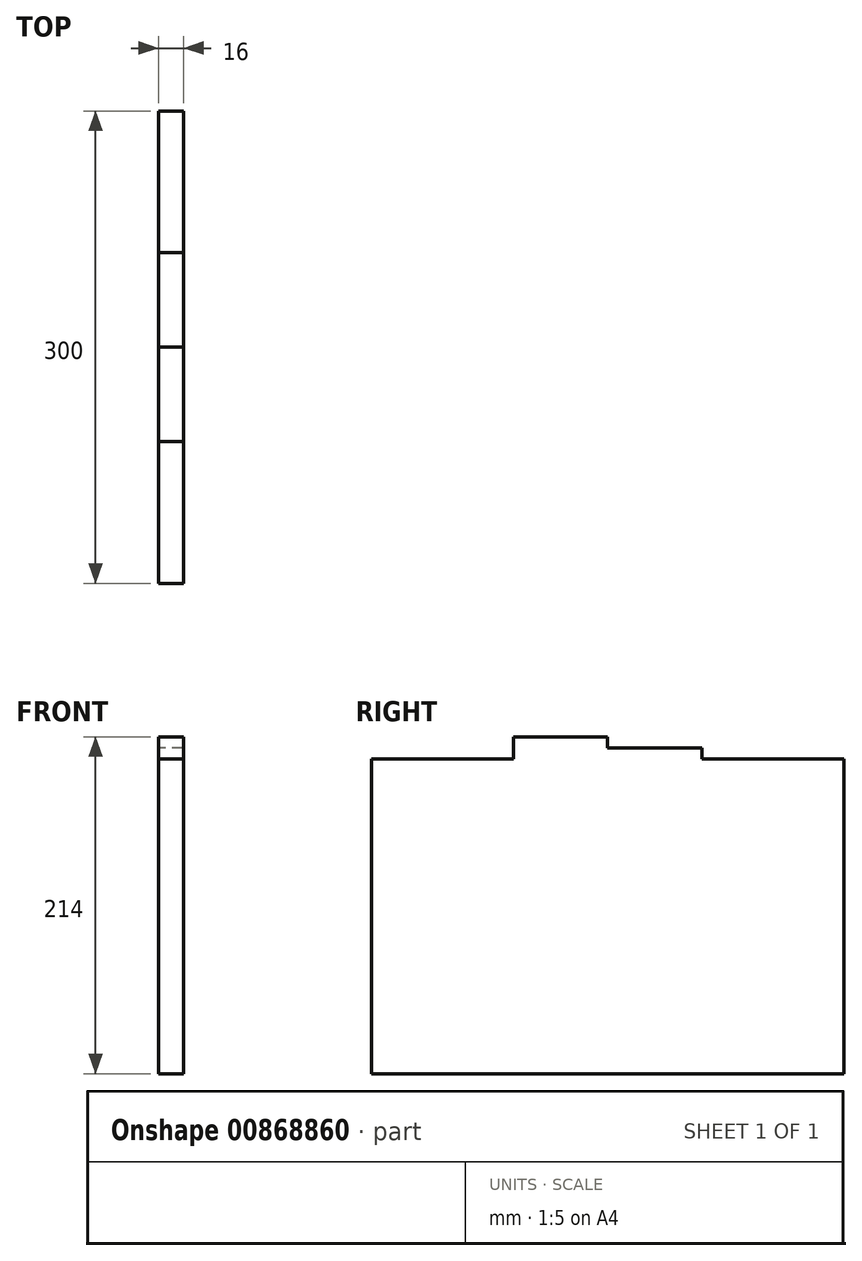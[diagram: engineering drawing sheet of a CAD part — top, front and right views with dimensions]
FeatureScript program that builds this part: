
annotation { "Feature Type Name" : "Feature", "Feature Type Description" : "" }
export const myFeature = defineFeature(function(context is Context, id is Id, definition is map)
    precondition{}
    {
        {
            var Q0;
            Q0=qCreatedBy(makeId("Right.planeOp"),FACE);
            var sketch = newSketch(context, id + "F0", { "sketchPlane" : qUnion([Q0])});
            skLineSegment(sketch, "E0.bottom", {"start": v(0, 0) * mm, "end": v(300, 0) * mm});
            skLineSegment(sketch, "E0.top", {"start": v(0, 200) * mm, "end": v(300, 200) * mm});
            skLineSegment(sketch, "E0.left", {"start": v(0, 0) * mm, "end": v(0, 200) * mm});
            skLineSegment(sketch, "E0.right", {"start": v(300, 0) * mm, "end": v(300, 200) * mm});
            skSolve(sketch);
        }
        {
            var Q0;
            Q0=makeQuery(id+"F0.imprint","IMPRINT",FACE,{"disambiguationData":[TD([[makeQuery(id+"F0.imprint","IMPRINT",EDGE,{"derivedFrom":sQuery(id+"F0.wireOp",EDGE,"E0.bottom")}),1.0]])]});
            extrude(context, id + "F1", {"entities" : qUnion([Q0]), "depth" : 16 * mm, "offsetDistance" : 25 * mm});
        }
        {
            var Q0;
            Q0=makeQuery(id+"F1.opExtrude","CAP_FACE",FACE,{"disambiguationData":[OSD([sQuery(id+"F0.wireOp",EDGE,"E0.bottom"),sQuery(id+"F0.wireOp",EDGE,"E0.top"),sQuery(id+"F0.wireOp",EDGE,"E0.left"),sQuery(id+"F0.wireOp",EDGE,"E0.right")])],"isStart":true});
            var sketch = newSketch(context, id + "F2", { "sketchPlane" : qUnion([Q0])});
            skLineSegment(sketch, "E1", {"start": v(-300, 200) * mm, "end": v(-210, 200) * mm});
            skLineSegment(sketch, "E2", {"start": v(-210, 200) * mm, "end": v(-210, 207) * mm});
            skLineSegment(sketch, "E3", {"start": v(-210, 207) * mm, "end": v(-150, 207) * mm});
            skLineSegment(sketch, "E4", {"start": v(-150, 207) * mm, "end": v(-150, 214) * mm});
            skLineSegment(sketch, "E5", {"start": v(-150, 214) * mm, "end": v(-90, 214) * mm});
            skLineSegment(sketch, "E6", {"start": v(-90, 214) * mm, "end": v(-90, 200) * mm});
            skLineSegment(sketch, "E7", {"start": v(-90, 200) * mm, "end": v(0, 200) * mm});
            skSolve(sketch);
        }
        {
            var Q0;
            {var subQ0=sQuery(id+"F2.wireOp",EDGE,"E2");Q0=makeQuery(id+"F2.imprint","IMPRINT",FACE,{"disambiguationData":[TD([[makeQuery(id+"F2.imprint","IMPRINT",EDGE,{"derivedFrom":subQ0}),-1.0]])]});}
            extrude(context, id + "F3", {"entities" : qUnion([Q0]), "operationType" : NewBodyOperationType.ADD, "oppositeDirection" : true, "depth" : 16 * mm, "offsetDistance" : 25 * mm});
        }
    });
